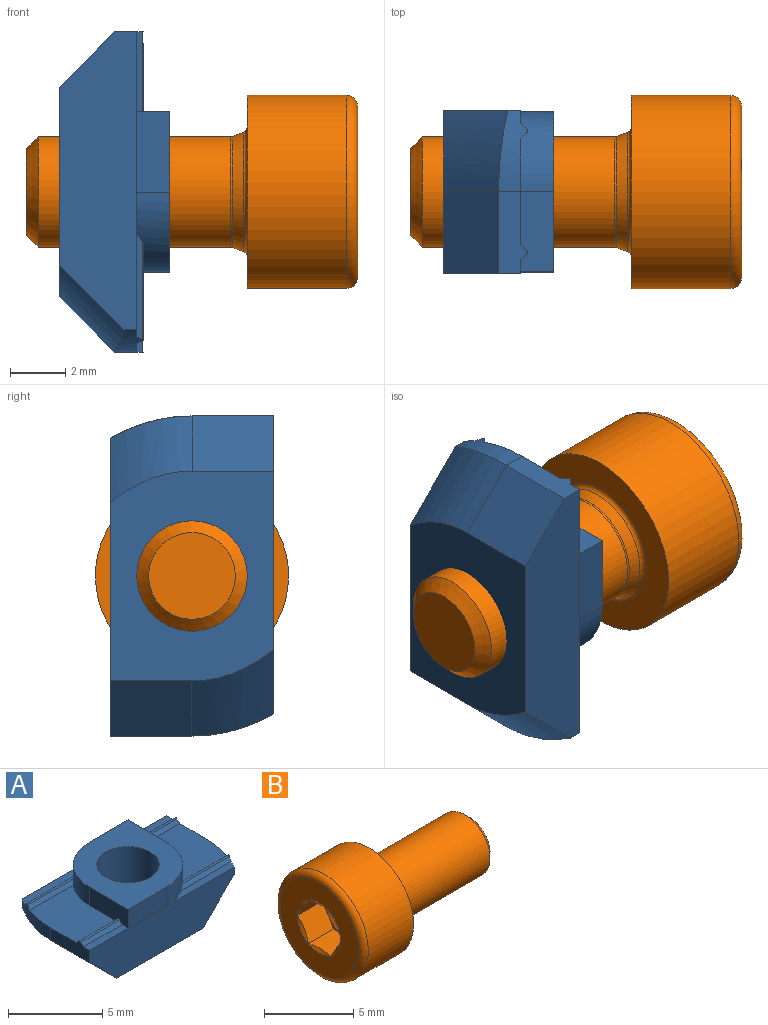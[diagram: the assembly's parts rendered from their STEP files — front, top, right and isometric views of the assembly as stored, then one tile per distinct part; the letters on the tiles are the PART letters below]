
ASSEMBLY  parts=2 mates=1
PART A: 35 faces, bbox 11.6x5.9x4.6 mm
  f0: cylinder r=1.65mm len=4mm, axis (0,0,1), area 41.5mm2, adj f7,f26
  f1: cylinder r=2.9mm len=2.9mm, axis (0,0,1), area 5.4mm2, adj f2,f5,f7,f8,f10,f12,f14,f33
  f2: plane 2.9x1.2mm, normal (1,0,0), area 3.4mm2, adj f1,f6,f7,f14,f16,f18,f20,f22
  f3: cylinder r=2.9mm len=2.9mm, axis (0,0,1), area 5.4mm2, adj f4,f6,f7,f15,f17,f19,f21,f22
  f4: plane 2.9x1.2mm, normal (-1,0,0), area 3.4mm2, adj f3,f5,f7,f9,f11,f13,f15,f33
  f5: plane 2.9x1.2mm, normal (0,-1,0), area 3.5mm2, adj f1,f4,f7,f33
  f6: plane 2.9x1.2mm, normal (0,1,0), area 3.5mm2, adj f2,f3,f7,f22
  f7: plane 5.8x5.8mm, normal (0,0,1), area 21.5mm2, adj f0,f1,f2,f3,f4,f5,f6
  f8: plane 3.83x0.21mm, normal (0,-0.71,0.71), area 1mm2, adj f1,f10,f32,f33
  f9: plane 2.9x0.2mm, normal (0,-0.71,0.71), area 0.8mm2, adj f4,f11,f30,f33
  f10: cylinder r=0.1mm len=3.59mm, axis (1,0,0), area 0.5mm2, adj f1,f8,f12,f32
  f11: cylinder r=0.1mm len=2.9mm, axis (1,0,0), area 0.5mm2, adj f4,f9,f13,f30
  f12: plane 3.51x0.21mm, normal (0,0.71,0.71), area 1mm2, adj f1,f10,f14,f32
  f13: plane 2.9x0.2mm, normal (0,0.71,0.71), area 0.8mm2, adj f4,f11,f15,f30
  f14: plane 3.85x3.63mm, normal (0,0,1), area 11.4mm2, adj f1,f2,f12,f16,f32,f34
  f15: plane 3.85x3.63mm, normal (0,0,1), area 11.4mm2, adj f3,f4,f13,f17,f29,f30
  f16: plane 2.9x0.2mm, normal (0,-0.71,0.71), area 0.8mm2, adj f2,f14,f18,f34
  f17: plane 3.51x0.21mm, normal (0,-0.71,0.71), area 1mm2, adj f3,f15,f19,f29
  f18: cylinder r=0.1mm len=2.9mm, axis (1,0,0), area 0.5mm2, adj f2,f16,f20,f34
  f19: cylinder r=0.1mm len=3.59mm, axis (1,0,0), area 0.5mm2, adj f3,f17,f21,f29
  f20: plane 2.9x0.2mm, normal (0,0.71,0.71), area 0.8mm2, adj f2,f18,f22,f34
  f21: plane 3.83x0.21mm, normal (0,0.71,0.71), area 1mm2, adj f3,f19,f22,f29
  f22: plane 11.05x0.48mm, normal (0,0,1), area 3.5mm2, adj f2,f3,f6,f20,f21,f25,f29,f34
  f23: plane 2.95x2mm, normal (0.71,0,-0.71), area 8.3mm2, adj f24,f25,f26,f34
  f24: cylinder r=5.8mm len=3.14mm, axis (0.71,0,0.71), area 9.2mm2, adj f23,f26,f31,f32
  f25: plane 10.79x2.8mm, normal (0,1,0), area 25.5mm2, adj f22,f23,f26,f28,f29,f34
  f26: plane 7.6x5.9mm, normal (0,0,-1), area 34.1mm2, adj f0,f23,f24,f25,f27,f28,f31
  f27: plane 2.95x2mm, normal (-0.71,0,-0.71), area 8.3mm2, adj f26,f28,f30,f31
  f28: cylinder r=5.8mm len=3.14mm, axis (-0.71,0,0.71), area 9.2mm2, adj f25,f26,f27,f29
  f29: cylinder r=5.8mm len=2.95mm, axis (0,0,1), area 2.2mm2, adj f15,f17,f19,f21,f22,f25,f28,f30
  f30: plane 2.95x1.03mm, normal (-1,0,0), area 2.4mm2, adj f9,f11,f13,f15,f27,f29,f31,f33
  f31: plane 10.79x2.8mm, normal (0,-1,0), area 25.5mm2, adj f24,f26,f27,f30,f32,f33
  f32: cylinder r=5.8mm len=2.95mm, axis (0,0,1), area 2.2mm2, adj f8,f10,f12,f14,f24,f31,f33,f34
  f33: plane 11.05x0.48mm, normal (0,0,1), area 3.5mm2, adj f1,f4,f5,f8,f9,f30,f31,f32
  f34: plane 2.95x1.03mm, normal (1,0,0), area 2.4mm2, adj f14,f16,f18,f20,f22,f23,f25,f32
PART B: 24 faces, bbox 12x7.6x7.6 mm
  f0: plane 1.3x0.75mm, normal (-1,0,0), area 0.1mm2, adj f16,f17,f23
  f1: plane 1.5x0.43mm, normal (-1,0,0), area 0.1mm2, adj f17,f18,f23
  f2: plane 1.3x0.75mm, normal (-1,0,0), area 0.1mm2, adj f18,f19,f23
  f3: plane 1.3x0.75mm, normal (-1,0,0), area 0.1mm2, adj f19,f20,f23
  f4: plane 1.5x0.43mm, normal (-1,0,0), area 0.1mm2, adj f20,f21,f23
  f5: cone r=1.74mm half-angle=60deg, axis (-1,0,0), area 2mm2, adj f15,f16,f17,f18,f19,f20,f21
  f6: cone r=2.01mm half-angle=20.6deg, axis (-1,0,0), area 5.6mm2, adj f7,f11
  f7: torus R=2.2mm, axis (1,0,0), area 0.9mm2, adj f6,f10
  f8: plane 3.14x3.14mm, normal (1,0,0), area 7.7mm2, adj f9
  f9: cone r=2mm half-angle=45deg, axis (-1,0,0), area 6.8mm2, adj f8,f10
  f10: cylinder r=2mm len=6.97mm, axis (1,0,0), area 87.6mm2, adj f7,f9
  f11: torus R=2.35mm, axis (1,0,0), area 3.4mm2, adj f6,f13
  f12: cylinder r=3.5mm len=7mm, axis (1,0,0), area 79.2mm2, adj f13,f14
  f13: plane 7x7mm, normal (1,0,0), area 21.1mm2, adj f11,f12
  f14: torus R=3.1mm, axis (1,0,0), area 13.2mm2, adj f12,f15
  f15: plane 6.2x6.2mm, normal (-1,0,0), area 20.7mm2, adj f5,f14
  f16: plane 2x1.74mm, normal (0,0,-1), area 3.3mm2, adj f0,f5,f17,f21,f22
  f17: plane 2x1.5mm, normal (0,0.87,-0.5), area 3.3mm2, adj f0,f1,f5,f16,f18
  f18: plane 2x1.5mm, normal (0,0.87,0.5), area 3.3mm2, adj f1,f2,f5,f17,f19
  f19: plane 2x1.74mm, normal (0,0,1), area 3.3mm2, adj f2,f3,f5,f18,f20
  f20: plane 2x1.5mm, normal (0,-0.87,0.5), area 3.3mm2, adj f3,f4,f5,f19,f21
  f21: plane 2x1.5mm, normal (0,-0.87,-0.5), area 3.3mm2, adj f4,f5,f16,f20,f22
  f22: plane 1.3x0.75mm, normal (-1,0,0), area 0.1mm2, adj f16,f21,f23
  f23: cone r=1.5mm half-angle=60deg, axis (-1,0,0), area 8.2mm2, adj f0,f1,f2,f3,f4,f22
PLACE A rot(axis=(-0.71,0,-0.71),180deg) t=(-8.49,-2.42,1.32)mm fixed
PLACE B rot(axis=(0,1,0),180deg) t=(-4.72,-2.42,1.32)mm
MATE fastened B.f5 <-> A.f1  axis (-1,0,0) through (-4.72,-2.42,1.32)mm
